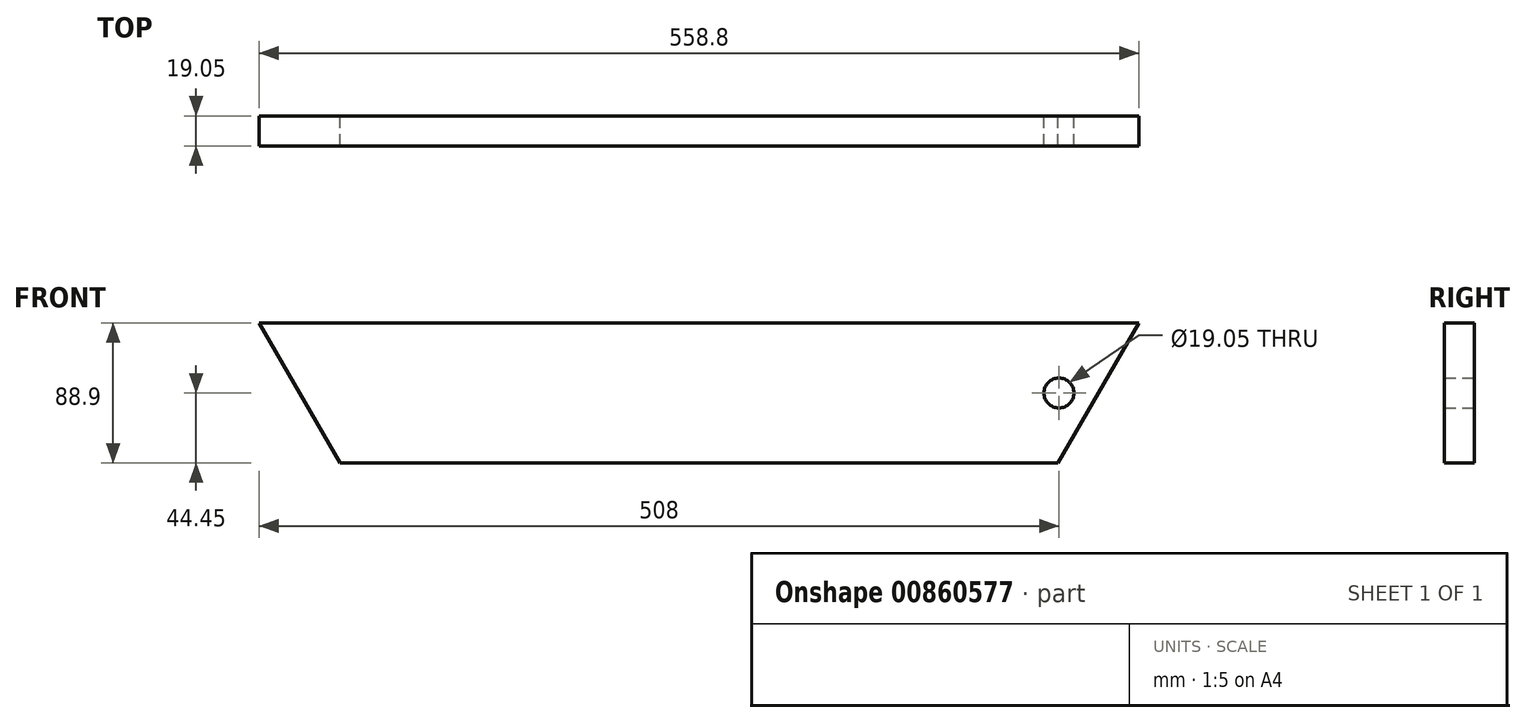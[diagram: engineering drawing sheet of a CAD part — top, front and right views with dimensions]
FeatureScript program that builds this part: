
annotation { "Feature Type Name" : "Feature", "Feature Type Description" : "" }
export const myFeature = defineFeature(function(context is Context, id is Id, definition is map)
    precondition{}
    {
        {
            var Q0;
            Q0=qCreatedBy(makeId("Front.planeOp"),FACE);
            var sketch = newSketch(context, id + "F0", { "sketchPlane" : qUnion([Q0])});
            skLineSegment(sketch, "E0.bottom", {"start": v(-51.33, 0) * mm, "end": v(-507.47, 0) * mm});
            skLineSegment(sketch, "E0.top", {"start": v(0, 88.9) * mm, "end": v(-558.8, 88.9) * mm});
            skLineSegment(sketch, "E0.left", {"start": v(0, 0) * mm, "end": v(0, 88.9) * mm});
            skLineSegment(sketch, "E1", {"start": v(0, 88.9) * mm, "end": v(-51.33, 0) * mm});
            skLineSegment(sketch, "E2", {"start": v(-558.8, 88.9) * mm, "end": v(-507.47, 0) * mm});
            skSolve(sketch);
        }
        {
            var Q0;
            Q0=makeQuery(id+"F0.imprint","IMPRINT",FACE,{"disambiguationData":[TD([[makeQuery(id+"F0.imprint","IMPRINT",EDGE,{"derivedFrom":sQuery(id+"F0.wireOp",EDGE,"E0.bottom")}),-1.0]])]});
            extrude(context, id + "F1", {"entities" : qUnion([Q0]), "depth" : 19.05 * mm, "offsetDistance" : 25.4 * mm});
        }
        {
            var Q0;
            Q0=qCreatedBy(makeId("Front.planeOp"),FACE);
            var sketch = newSketch(context, id + "F2", { "sketchPlane" : qUnion([Q0])});
            skCircle(sketch, "E3", {"center": v(-50.8, 44.45) * mm, "radius": 9.53 * mm});
            skSolve(sketch);
        }
        {
            var Q0;
            Q0=sQuery(id+"F2.wireOp",VERTEX,"E3.center");
            var Q1;
            Q1=makeQuery(id+"F1.opExtrude","SWEPT_BODY",BODY,{"disambiguationData":[OSD([sQuery(id+"F0.wireOp",EDGE,"E0.bottom"),sQuery(id+"F0.wireOp",EDGE,"E0.top"),sQuery(id+"F0.wireOp",EDGE,"E1"),sQuery(id+"F0.wireOp",EDGE,"E2")])]});
            hole(context, id + "F3", {"style" : HoleStyle.SIMPLE, "endStyle" : HoleEndStyle.THROUGH, "oppositeDirection" : true, "holeDiameter" : 19.05 * mm, "majorDiameter" : 6.35 * mm, "isTappedThrough" : true, "tappedDepth" : 12.7 * mm, "tapClearance" : 3, "locations" : qUnion([Q0]), "scope" : qUnion([Q1])});
        }
    });
